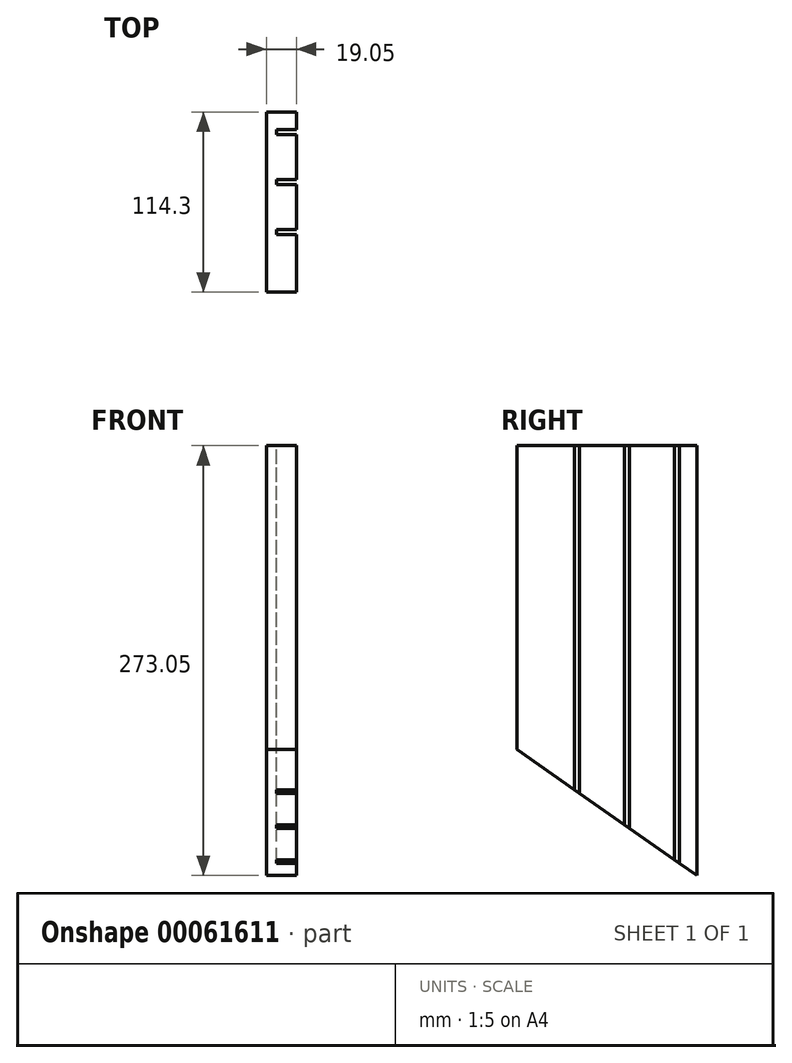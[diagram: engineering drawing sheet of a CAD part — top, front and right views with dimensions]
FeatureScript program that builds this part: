
annotation { "Feature Type Name" : "Feature", "Feature Type Description" : "" }
export const myFeature = defineFeature(function(context is Context, id is Id, definition is map)
    precondition{}
    {
        {
            var Q0;
            Q0=qCreatedBy(makeId("Right.planeOp"),FACE);
            var sketch = newSketch(context, id + "F0", { "sketchPlane" : qUnion([Q0])});
            skLineSegment(sketch, "E0.bottom", {"start": v(0, 0) * mm, "end": v(-114.3, 0) * mm});
            skLineSegment(sketch, "E0.top", {"start": v(0, -273.05) * mm, "end": v(-114.3, -273.05) * mm});
            skLineSegment(sketch, "E0.left", {"start": v(0, 0) * mm, "end": v(0, -273.05) * mm});
            skLineSegment(sketch, "E0.right", {"start": v(-114.3, 0) * mm, "end": v(-114.3, -273.05) * mm});
            skSolve(sketch);
        }
        {
            var Q0;
            Q0 = qSketchRegion(id + "F0", true);
            extrude(context, id + "F1", {"entities" : qUnion([Q0]), "depth" : 19.05 * mm});
        }
        {
            var Q0;
            Q0=makeQuery(id+"F1.opExtrude","CAP_FACE",FACE,{"disambiguationData":[OSD([sQuery(id+"F0.wireOp",EDGE,"E0.bottom"),sQuery(id+"F0.wireOp",EDGE,"E0.top"),sQuery(id+"F0.wireOp",EDGE,"E0.left"),sQuery(id+"F0.wireOp",EDGE,"E0.right")])],"isStart":false});
            var sketch = newSketch(context, id + "F2", { "sketchPlane" : qUnion([Q0])});
            skLineSegment(sketch, "E1.bottom", {"start": v(-11.11, -273.05) * mm, "end": v(-14.29, -273.05) * mm});
            skLineSegment(sketch, "E1.top", {"start": v(-11.11, 0) * mm, "end": v(-14.29, 0) * mm});
            skLineSegment(sketch, "E1.left", {"start": v(-11.11, -273.05) * mm, "end": v(-11.11, 0) * mm});
            skLineSegment(sketch, "E1.right", {"start": v(-14.29, -273.05) * mm, "end": v(-14.29, 0) * mm});
            skLineSegment(sketch, "E2.bottom", {"start": v(-42.86, -273.05) * mm, "end": v(-46.04, -273.05) * mm});
            skLineSegment(sketch, "E2.top", {"start": v(-42.86, 0) * mm, "end": v(-46.04, 0) * mm});
            skLineSegment(sketch, "E2.left", {"start": v(-42.86, -273.05) * mm, "end": v(-42.86, 0) * mm});
            skLineSegment(sketch, "E2.right", {"start": v(-46.04, -273.05) * mm, "end": v(-46.04, 0) * mm});
            skLineSegment(sketch, "E3.bottom", {"start": v(-74.61, -273.05) * mm, "end": v(-77.79, -273.05) * mm});
            skLineSegment(sketch, "E3.top", {"start": v(-74.61, 0) * mm, "end": v(-77.79, 0) * mm});
            skLineSegment(sketch, "E3.left", {"start": v(-74.61, -273.05) * mm, "end": v(-74.61, 0) * mm});
            skLineSegment(sketch, "E3.right", {"start": v(-77.79, -273.05) * mm, "end": v(-77.79, 0) * mm});
            skLineSegment(sketch, "E4", {"start": v(-114.3, -12.6) * mm, "end": v(-57.15, -12.6) * mm, "construction": true});
            skLineSegment(sketch, "E5", {"start": v(-57.15, -12.6) * mm, "end": v(-57.15, 15.51) * mm, "construction": true});
            skLineSegment(sketch, "E6", {"start": v(-57.15, -12.6) * mm, "end": v(0, -12.6) * mm, "construction": true});
            skSolve(sketch);
        }
        {
            var Q0;
            Q0 = qSketchRegion(id + "F2", true);
            extrude(context, id + "F3", {"entities" : qUnion([Q0]), "operationType" : NewBodyOperationType.REMOVE, "oppositeDirection" : true, "depth" : 12.7 * mm});
        }
        {
            var Q0;
            Q0=qCreatedBy(makeId("Right.planeOp"),FACE);
            var sketch = newSketch(context, id + "F4", { "sketchPlane" : qUnion([Q0])});
            skLineSegment(sketch, "E7", {"start": v(0, -273.05) * mm, "end": v(-114.3, -193.02) * mm});
            skLineSegment(sketch, "E8", {"start": v(-114.3, -193.02) * mm, "end": v(-114.3, -273.05) * mm});
            skLineSegment(sketch, "E9", {"start": v(-114.3, -273.05) * mm, "end": v(0, -273.05) * mm});
            skSolve(sketch);
        }
        {
            var Q0;
            Q0 = qSketchRegion(id + "F4", true);
            extrude(context, id + "F5", {"entities" : qUnion([Q0]), "operationType" : NewBodyOperationType.REMOVE, "endBound" : BoundingType.THROUGH_ALL, "depth" : 25.4 * mm});
        }
    });
